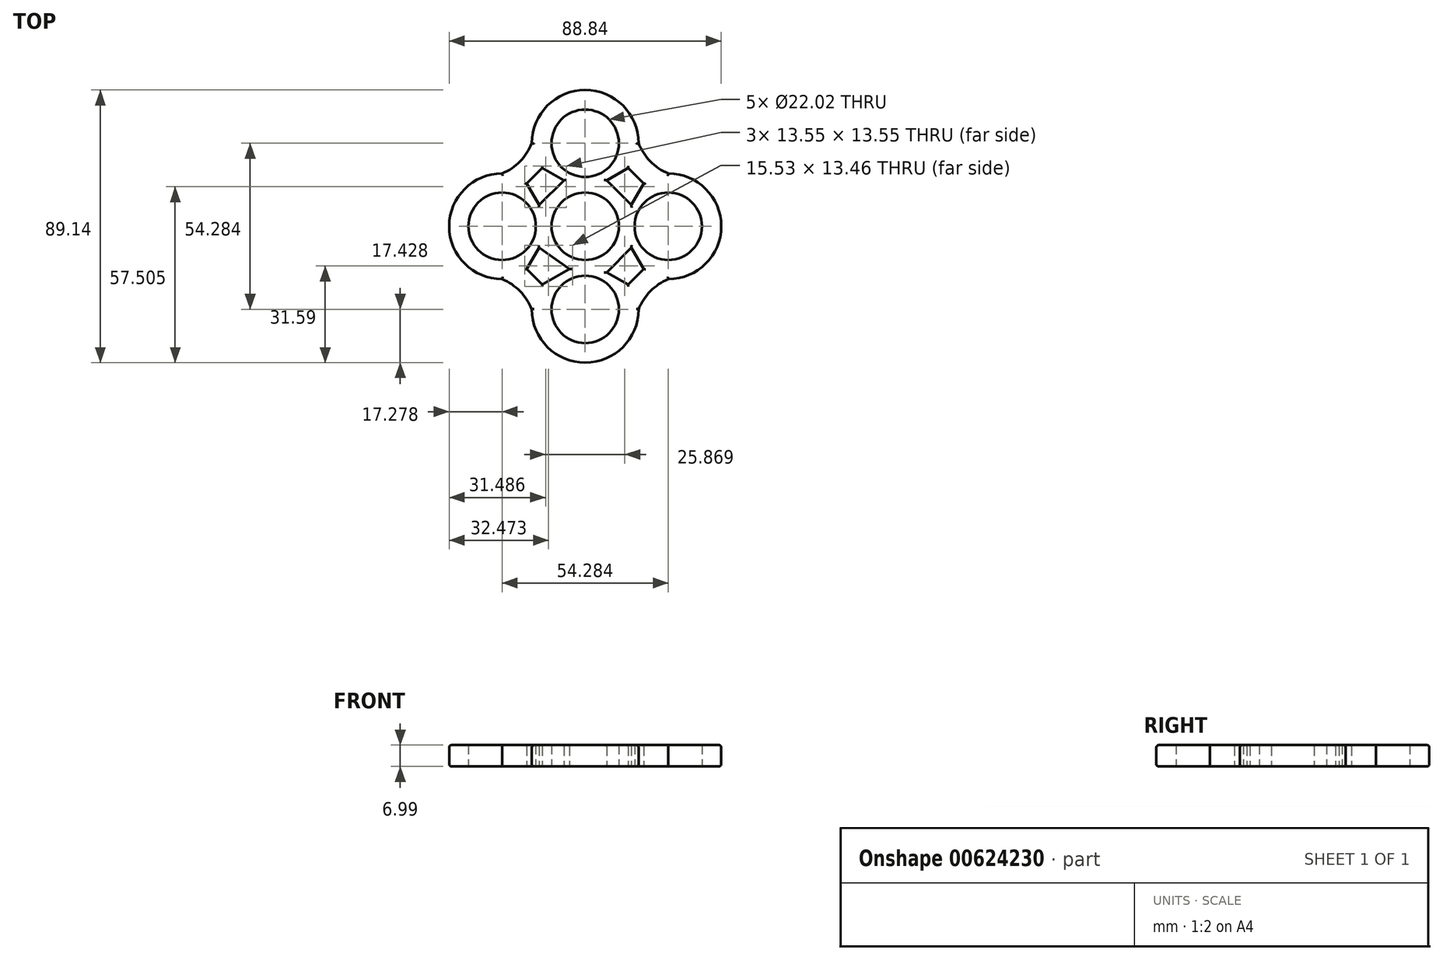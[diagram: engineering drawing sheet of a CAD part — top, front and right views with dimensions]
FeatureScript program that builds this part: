
annotation { "Feature Type Name" : "Feature", "Feature Type Description" : "" }
export const myFeature = defineFeature(function(context is Context, id is Id, definition is map)
    precondition{}
    {
        {
            var Q0;
            Q0=qCreatedBy(makeId("Top.planeOp"),FACE);
            var sketch = newSketch(context, id + "F0", { "sketchPlane" : qUnion([Q0])});
            skCircle(sketch, "E0", {"center": v(0, 0) * mm, "radius": 11.01 * mm});
            skCircle(sketch, "E1", {"center": v(27.14, 0) * mm, "radius": 11.01 * mm});
            skCircle(sketch, "E2", {"center": v(0, 27.14) * mm, "radius": 11.01 * mm});
            skCircle(sketch, "E3", {"center": v(0, -27.14) * mm, "radius": 11.01 * mm});
            skCircle(sketch, "E4", {"center": v(-27.14, 0) * mm, "radius": 11.01 * mm});
            skArc(sketch, "E5", {"start": v(-27.14, 17.28) * mm, "mid": v(-21.29, 21.23) * mm, "end": v(-17.43, 27.14) * mm});
            skArc(sketch, "E6", {"start": v(-17.43, -27.14) * mm, "mid": v(-21.29, -21.23) * mm, "end": v(-27.14, -17.28) * mm});
            skArc(sketch, "E7", {"start": v(17.43, 27.14) * mm, "mid": v(21.29, 21.23) * mm, "end": v(27.14, 17.28) * mm});
            skArc(sketch, "E8", {"start": v(27.14, -17.28) * mm, "mid": v(21.29, -21.23) * mm, "end": v(17.43, -27.14) * mm});
            skArc(sketch, "E9", {"start": v(-27.14, 17.28) * mm, "mid": v(-44.42, 0) * mm, "end": v(-27.14, -17.28) * mm});
            skArc(sketch, "E10", {"start": v(17.43, 27.14) * mm, "mid": v(0, 44.57) * mm, "end": v(-17.43, 27.14) * mm});
            skArc(sketch, "E11", {"start": v(27.14, -17.28) * mm, "mid": v(44.42, 0) * mm, "end": v(27.14, 17.28) * mm});
            skArc(sketch, "E12", {"start": v(-17.43, -27.14) * mm, "mid": v(0, -44.57) * mm, "end": v(17.43, -27.14) * mm});
            skCircle(sketch, "E13.cCircle", {"center": v(-27.14, 0) * mm, "radius": 13.97 * mm, "construction": true});
            skLineSegment(sketch, "E13.0", {"start": v(-19.08, 13.97) * mm, "end": v(-11.01, 0) * mm});
            skLineSegment(sketch, "E13.1", {"start": v(-11.01, 0) * mm, "end": v(-19.08, -13.97) * mm});
            skLineSegment(sketch, "E13.2", {"start": v(-19.08, -13.97) * mm, "end": v(-35.2, -13.97) * mm});
            skLineSegment(sketch, "E13.3", {"start": v(-35.2, -13.97) * mm, "end": v(-43.27, 0) * mm});
            skLineSegment(sketch, "E13.4", {"start": v(-43.27, 0) * mm, "end": v(-35.2, 13.97) * mm});
            skLineSegment(sketch, "E13.5", {"start": v(-35.2, 13.97) * mm, "end": v(-19.08, 13.97) * mm});
            skPoint(sketch, "E13.0.midPoint", {"position": v(-15.04, 6.99) * mm});
            skCircle(sketch, "E14.cCircle", {"center": v(0, 27.14) * mm, "radius": 13.97 * mm, "construction": true});
            skLineSegment(sketch, "E14.0", {"start": v(13.97, 35.2) * mm, "end": v(13.97, 19.08) * mm});
            skLineSegment(sketch, "E14.1", {"start": v(13.97, 19.08) * mm, "end": v(0, 11.01) * mm});
            skLineSegment(sketch, "E14.2", {"start": v(0, 11.01) * mm, "end": v(-13.97, 19.08) * mm});
            skLineSegment(sketch, "E14.3", {"start": v(-13.97, 19.08) * mm, "end": v(-13.97, 35.2) * mm});
            skLineSegment(sketch, "E14.4", {"start": v(-13.97, 35.2) * mm, "end": v(0, 43.27) * mm});
            skLineSegment(sketch, "E14.5", {"start": v(0, 43.27) * mm, "end": v(13.97, 35.2) * mm});
            skPoint(sketch, "E14.0.midPoint", {"position": v(13.97, 27.14) * mm});
            skCircle(sketch, "E15.cCircle", {"center": v(27.14, 0) * mm, "radius": 13.97 * mm, "construction": true});
            skLineSegment(sketch, "E15.0", {"start": v(35.2, 13.97) * mm, "end": v(43.27, 0) * mm});
            skLineSegment(sketch, "E15.1", {"start": v(43.27, 0) * mm, "end": v(35.2, -13.97) * mm});
            skLineSegment(sketch, "E15.2", {"start": v(35.2, -13.97) * mm, "end": v(19.08, -13.97) * mm});
            skLineSegment(sketch, "E15.3", {"start": v(19.08, -13.97) * mm, "end": v(11.01, 0) * mm});
            skLineSegment(sketch, "E15.4", {"start": v(11.01, 0) * mm, "end": v(19.08, 13.97) * mm});
            skLineSegment(sketch, "E15.5", {"start": v(19.08, 13.97) * mm, "end": v(35.2, 13.97) * mm});
            skPoint(sketch, "E15.0.midPoint", {"position": v(39.24, 6.98) * mm});
            skCircle(sketch, "E16.cCircle", {"center": v(0, -27.14) * mm, "radius": 13.97 * mm, "construction": true});
            skLineSegment(sketch, "E16.0", {"start": v(13.97, -19.08) * mm, "end": v(13.97, -35.2) * mm});
            skLineSegment(sketch, "E16.1", {"start": v(13.97, -35.2) * mm, "end": v(0, -43.27) * mm});
            skLineSegment(sketch, "E16.2", {"start": v(0, -43.27) * mm, "end": v(-13.97, -35.2) * mm});
            skLineSegment(sketch, "E16.3", {"start": v(-13.97, -35.2) * mm, "end": v(-13.97, -19.08) * mm});
            skLineSegment(sketch, "E16.4", {"start": v(-13.97, -19.08) * mm, "end": v(0, -11.01) * mm});
            skLineSegment(sketch, "E16.5", {"start": v(0, -11.01) * mm, "end": v(13.97, -19.08) * mm});
            skPoint(sketch, "E16.0.midPoint", {"position": v(13.97, -27.14) * mm});
            skPoint(sketch, "E17.0.midPoint", {"position": v(15.04, 6.99) * mm});
            skLineSegment(sketch, "E18", {"start": v(-19.08, 13.97) * mm, "end": v(-13.97, 19.08) * mm});
            skLineSegment(sketch, "E19", {"start": v(13.97, 19.08) * mm, "end": v(19.08, 13.97) * mm});
            skLineSegment(sketch, "E20", {"start": v(-19.08, -13.97) * mm, "end": v(-13.97, -19.08) * mm});
            skLineSegment(sketch, "E21", {"start": v(13.97, -19.08) * mm, "end": v(19.08, -13.97) * mm});
            skPoint(sketch, "E22.startSnap0", {"position": v(15.04, -6.98) * mm});
            skLineSegment(sketch, "E23", {"start": v(-6.99, 15.04) * mm, "end": v(-15.04, 6.99) * mm});
            skLineSegment(sketch, "E24", {"start": v(15.04, -6.98) * mm, "end": v(6.99, -15.04) * mm});
            skLineSegment(sketch, "E25", {"start": v(-15.04, -6.98) * mm, "end": v(-5.13, -13.97) * mm});
            skLineSegment(sketch, "E26", {"start": v(6.98, 15.04) * mm, "end": v(15.04, 6.98) * mm});
            skLineSegment(sketch, "E27", {"start": v(0, -27.14) * mm, "end": v(0, 0) * mm});
            skLineSegment(sketch, "E28", {"start": v(0, 0) * mm, "end": v(27.14, 0) * mm});
            skLineSegment(sketch, "E29", {"start": v(0, 27.14) * mm, "end": v(0, 0) * mm});
            skLineSegment(sketch, "E30", {"start": v(-27.14, 0) * mm, "end": v(0, 0) * mm});
            skSolve(sketch);
        }
        {
            var Q0;
            Q0=makeQuery(id+"F0.imprint","IMPRINT",FACE,{"disambiguationData":[TD([[makeQuery(id+"F0.imprint","IMPRINT",EDGE,{"derivedFrom":sQuery(id+"F0.wireOp",EDGE,"E4")}),-1.0]])]});
            var Q1;
            Q1=makeQuery(id+"F0.imprint","IMPRINT",FACE,{"disambiguationData":[TD([[makeQuery(id+"F0.imprint","IMPRINT",EDGE,{"derivedFrom":sQuery(id+"F0.wireOp",EDGE,"E3")}),-1.0]])]});
            var Q2;
            Q2=makeQuery(id+"F0.imprint","IMPRINT",FACE,{"disambiguationData":[TD([[makeQuery(id+"F0.imprint","IMPRINT",EDGE,{"derivedFrom":sQuery(id+"F0.wireOp",EDGE,"E1")}),-1.0]])]});
            var Q3;
            Q3=makeQuery(id+"F0.imprint","IMPRINT",FACE,{"disambiguationData":[TD([[makeQuery(id+"F0.imprint","IMPRINT",EDGE,{"derivedFrom":sQuery(id+"F0.wireOp",EDGE,"E2")}),-1.0]])]});
            var Q4;
            {var subQ5=sQuery(id+"F0.wireOp",EDGE,"E26");Q4=makeQuery(id+"F0.imprint","IMPRINT",FACE,{"disambiguationData":[TD([[makeQuery(id+"F0.imprint","IMPRINT",EDGE,{"derivedFrom":subQ5}),-1.0]])]});}
            var Q5;
            {var subQ5=sQuery(id+"F0.wireOp",EDGE,"E23");Q5=makeQuery(id+"F0.imprint","IMPRINT",FACE,{"disambiguationData":[TD([[makeQuery(id+"F0.imprint","IMPRINT",EDGE,{"derivedFrom":subQ5}),1.0]])]});}
            var Q6;
            {var subQ5=sQuery(id+"F0.wireOp",EDGE,"E25");Q6=makeQuery(id+"F0.imprint","IMPRINT",FACE,{"disambiguationData":[TD([[makeQuery(id+"F0.imprint","IMPRINT",EDGE,{"derivedFrom":subQ5}),1.0]])]});}
            var Q7;
            {var subQ5=sQuery(id+"F0.wireOp",EDGE,"E24");Q7=makeQuery(id+"F0.imprint","IMPRINT",FACE,{"disambiguationData":[TD([[makeQuery(id+"F0.imprint","IMPRINT",EDGE,{"derivedFrom":subQ5}),-1.0]])]});}
            var Q8;
            Q8=makeQuery(id+"F0.imprint","IMPRINT",FACE,{"disambiguationData":[TD([[makeQuery(id+"F0.imprint","IMPRINT",EDGE,{"derivedFrom":sQuery(id+"F0.wireOp",EDGE,"E5")}),-1.0]])]});
            extrude(context, id + "F1", {"entities" : qUnion([Q0, Q1, Q2, Q3, Q4, Q5, Q6, Q7, Q8]), "depth" : 7 * mm, "offsetDistance" : 25.4 * mm});
        }
        {
            var Q0;
            Q0=makeQuery(id+"F1.opExtrude","CAP_EDGE",EDGE,{"disambiguationData":[OSD([sQuery(id+"F0.wireOp",EDGE,"E5")])],"isStart":false});
            var Q1;
            Q1=makeQuery(id+"F1.opExtrude","CAP_EDGE",EDGE,{"disambiguationData":[OSD([sQuery(id+"F0.wireOp",EDGE,"E6")])],"isStart":false});
            var Q2;
            Q2=makeQuery(id+"F1.opExtrude","CAP_EDGE",EDGE,{"disambiguationData":[OSD([sQuery(id+"F0.wireOp",EDGE,"E9")])],"isStart":false});
            var Q3;
            Q3=makeQuery(id+"F1.opExtrude","CAP_EDGE",EDGE,{"disambiguationData":[OSD([sQuery(id+"F0.wireOp",EDGE,"E12")])],"isStart":false});
            var Q4;
            Q4=makeQuery(id+"F1.opExtrude","CAP_EDGE",EDGE,{"disambiguationData":[OSD([sQuery(id+"F0.wireOp",EDGE,"E8")])],"isStart":false});
            var Q5;
            Q5=makeQuery(id+"F1.opExtrude","CAP_EDGE",EDGE,{"disambiguationData":[OSD([sQuery(id+"F0.wireOp",EDGE,"E11")])],"isStart":false});
            var Q6;
            Q6=makeQuery(id+"F1.opExtrude","CAP_EDGE",EDGE,{"disambiguationData":[OSD([sQuery(id+"F0.wireOp",EDGE,"E7")])],"isStart":false});
            var Q7;
            Q7=makeQuery(id+"F1.opExtrude","CAP_EDGE",EDGE,{"disambiguationData":[OSD([sQuery(id+"F0.wireOp",EDGE,"E10")])],"isStart":false});
            var Q8;
            Q8=makeQuery(id+"F1.opExtrude","CAP_EDGE",EDGE,{"disambiguationData":[OSD([sQuery(id+"F0.wireOp",EDGE,"E9")])],"isStart":true});
            var Q9;
            Q9=makeQuery(id+"F1.opExtrude","CAP_EDGE",EDGE,{"disambiguationData":[OSD([sQuery(id+"F0.wireOp",EDGE,"E10")])],"isStart":true});
            var Q10;
            Q10=makeQuery(id+"F1.opExtrude","CAP_EDGE",EDGE,{"disambiguationData":[OSD([sQuery(id+"F0.wireOp",EDGE,"E5")])],"isStart":true});
            var Q11;
            Q11=makeQuery(id+"F1.opExtrude","CAP_EDGE",EDGE,{"disambiguationData":[OSD([sQuery(id+"F0.wireOp",EDGE,"E7")])],"isStart":true});
            var Q12;
            Q12=makeQuery(id+"F1.opExtrude","CAP_EDGE",EDGE,{"disambiguationData":[OSD([sQuery(id+"F0.wireOp",EDGE,"E6")])],"isStart":true});
            var Q13;
            Q13=makeQuery(id+"F1.opExtrude","CAP_EDGE",EDGE,{"disambiguationData":[OSD([sQuery(id+"F0.wireOp",EDGE,"E12")])],"isStart":true});
            var Q14;
            Q14=makeQuery(id+"F1.opExtrude","CAP_EDGE",EDGE,{"disambiguationData":[OSD([sQuery(id+"F0.wireOp",EDGE,"E8")])],"isStart":true});
            var Q15;
            Q15=makeQuery(id+"F1.opExtrude","CAP_EDGE",EDGE,{"disambiguationData":[OSD([sQuery(id+"F0.wireOp",EDGE,"E11")])],"isStart":true});
            fillet(context, id + "F2", {"entities" : qUnion([Q0, Q1, Q2, Q3, Q4, Q5, Q6, Q7, Q8, Q9, Q10, Q11, Q12, Q13, Q14, Q15]), "radius" : 0.76 * mm, "tangentPropagation" : true, "allowEdgeOverflow" : false});
        }
        {
            var Q0;
            Q0=makeQuery(id+"F1.opExtrude","CAP_EDGE",EDGE,{"disambiguationData":[OSD([sQuery(id+"F0.wireOp",EDGE,"E20")])],"isStart":false});
            var Q1;
            Q1=makeQuery(id+"F1.opExtrude","CAP_EDGE",EDGE,{"disambiguationData":[OSD([sQuery(id+"F0.wireOp",EDGE,"E13.1")])],"isStart":false});
            var Q2;
            Q2=makeQuery(id+"F1.opExtrude","CAP_EDGE",EDGE,{"disambiguationData":[OSD([sQuery(id+"F0.wireOp",EDGE,"E25")])],"isStart":false});
            var Q3;
            Q3=makeQuery(id+"F1.opExtrude","CAP_EDGE",EDGE,{"disambiguationData":[OSD([sQuery(id+"F0.wireOp",EDGE,"E16.4")])],"isStart":false});
            var Q4;
            Q4=makeQuery(id+"F1.opExtrude","CAP_EDGE",EDGE,{"disambiguationData":[OSD([sQuery(id+"F0.wireOp",EDGE,"E24")])],"isStart":false});
            var Q5;
            Q5=makeQuery(id+"F1.opExtrude","CAP_EDGE",EDGE,{"disambiguationData":[OSD([sQuery(id+"F0.wireOp",EDGE,"E16.5")])],"isStart":false});
            var Q6;
            Q6=makeQuery(id+"F1.opExtrude","CAP_EDGE",EDGE,{"disambiguationData":[OSD([sQuery(id+"F0.wireOp",EDGE,"E21")])],"isStart":false});
            var Q7;
            Q7=makeQuery(id+"F1.opExtrude","CAP_EDGE",EDGE,{"disambiguationData":[OSD([sQuery(id+"F0.wireOp",EDGE,"E15.3")])],"isStart":false});
            var Q8;
            Q8=makeQuery(id+"F1.opExtrude","CAP_EDGE",EDGE,{"disambiguationData":[OSD([sQuery(id+"F0.wireOp",EDGE,"E15.4")])],"isStart":false});
            var Q9;
            Q9=makeQuery(id+"F1.opExtrude","CAP_EDGE",EDGE,{"disambiguationData":[OSD([sQuery(id+"F0.wireOp",EDGE,"E26")])],"isStart":false});
            var Q10;
            Q10=makeQuery(id+"F1.opExtrude","CAP_EDGE",EDGE,{"disambiguationData":[OSD([sQuery(id+"F0.wireOp",EDGE,"E14.1")])],"isStart":false});
            var Q11;
            Q11=makeQuery(id+"F1.opExtrude","CAP_EDGE",EDGE,{"disambiguationData":[OSD([sQuery(id+"F0.wireOp",EDGE,"E19")])],"isStart":false});
            var Q12;
            Q12=makeQuery(id+"F1.opExtrude","CAP_EDGE",EDGE,{"disambiguationData":[OSD([sQuery(id+"F0.wireOp",EDGE,"E23")])],"isStart":false});
            var Q13;
            Q13=makeQuery(id+"F1.opExtrude","CAP_EDGE",EDGE,{"disambiguationData":[OSD([sQuery(id+"F0.wireOp",EDGE,"E18")])],"isStart":false});
            var Q14;
            Q14=makeQuery(id+"F1.opExtrude","CAP_EDGE",EDGE,{"disambiguationData":[OSD([sQuery(id+"F0.wireOp",EDGE,"E13.0")])],"isStart":false});
            var Q15;
            Q15=makeQuery(id+"F1.opExtrude","CAP_EDGE",EDGE,{"disambiguationData":[OSD([sQuery(id+"F0.wireOp",EDGE,"E14.2")])],"isStart":true});
            var Q16;
            Q16=makeQuery(id+"F1.opExtrude","CAP_EDGE",EDGE,{"disambiguationData":[OSD([sQuery(id+"F0.wireOp",EDGE,"E14.2")])],"isStart":false});
            var Q17;
            Q17=makeQuery(id+"F1.opExtrude","CAP_EDGE",EDGE,{"disambiguationData":[OSD([sQuery(id+"F0.wireOp",EDGE,"E23")])],"isStart":true});
            var Q18;
            Q18=makeQuery(id+"F1.opExtrude","CAP_EDGE",EDGE,{"disambiguationData":[OSD([sQuery(id+"F0.wireOp",EDGE,"E13.0")])],"isStart":true});
            var Q19;
            Q19=makeQuery(id+"F1.opExtrude","CAP_EDGE",EDGE,{"disambiguationData":[OSD([sQuery(id+"F0.wireOp",EDGE,"E18")])],"isStart":true});
            var Q20;
            Q20=makeQuery(id+"F1.opExtrude","CAP_EDGE",EDGE,{"disambiguationData":[OSD([sQuery(id+"F0.wireOp",EDGE,"E13.1")])],"isStart":true});
            var Q21;
            Q21=makeQuery(id+"F1.opExtrude","CAP_EDGE",EDGE,{"disambiguationData":[OSD([sQuery(id+"F0.wireOp",EDGE,"E20")])],"isStart":true});
            var Q22;
            Q22=makeQuery(id+"F1.opExtrude","CAP_EDGE",EDGE,{"disambiguationData":[OSD([sQuery(id+"F0.wireOp",EDGE,"E16.4")])],"isStart":true});
            var Q23;
            Q23=makeQuery(id+"F1.opExtrude","CAP_EDGE",EDGE,{"disambiguationData":[OSD([sQuery(id+"F0.wireOp",EDGE,"E25")])],"isStart":true});
            var Q24;
            Q24=makeQuery(id+"F1.opExtrude","CAP_EDGE",EDGE,{"disambiguationData":[OSD([sQuery(id+"F0.wireOp",EDGE,"E24")])],"isStart":true});
            var Q25;
            Q25=makeQuery(id+"F1.opExtrude","CAP_EDGE",EDGE,{"disambiguationData":[OSD([sQuery(id+"F0.wireOp",EDGE,"E16.5")])],"isStart":true});
            var Q26;
            Q26=makeQuery(id+"F1.opExtrude","CAP_EDGE",EDGE,{"disambiguationData":[OSD([sQuery(id+"F0.wireOp",EDGE,"E21")])],"isStart":true});
            var Q27;
            Q27=makeQuery(id+"F1.opExtrude","CAP_EDGE",EDGE,{"disambiguationData":[OSD([sQuery(id+"F0.wireOp",EDGE,"E15.3")])],"isStart":true});
            var Q28;
            Q28=makeQuery(id+"F1.opExtrude","CAP_EDGE",EDGE,{"disambiguationData":[OSD([sQuery(id+"F0.wireOp",EDGE,"E26")])],"isStart":true});
            var Q29;
            Q29=makeQuery(id+"F1.opExtrude","CAP_EDGE",EDGE,{"disambiguationData":[OSD([sQuery(id+"F0.wireOp",EDGE,"E14.1")])],"isStart":true});
            var Q30;
            Q30=makeQuery(id+"F1.opExtrude","CAP_EDGE",EDGE,{"disambiguationData":[OSD([sQuery(id+"F0.wireOp",EDGE,"E19")])],"isStart":true});
            var Q31;
            Q31=makeQuery(id+"F1.opExtrude","CAP_EDGE",EDGE,{"disambiguationData":[OSD([sQuery(id+"F0.wireOp",EDGE,"E15.4")])],"isStart":true});
            fillet(context, id + "F3", {"entities" : qUnion([Q0, Q1, Q2, Q3, Q4, Q5, Q6, Q7, Q8, Q9, Q10, Q11, Q12, Q13, Q14, Q15, Q16, Q17, Q18, Q19, Q20, Q21, Q22, Q23, Q24, Q25, Q26, Q27, Q28, Q29, Q30, Q31]), "radius" : 0.5 * mm, "tangentPropagation" : true, "allowEdgeOverflow" : false});
        }
    });
